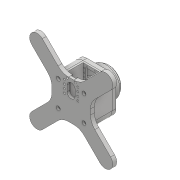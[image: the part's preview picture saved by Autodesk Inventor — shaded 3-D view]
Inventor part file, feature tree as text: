
AUTODESK INVENTOR PART (.ipt)
format: ipt  version: 2017 (Build 210142000, 142)  size: 484,864 bytes
history: native  units: mm
features: sketch x17, extrude x13, hole x4, fillet x2, projected_geometry x2, other x2, plane x1, split x1, chamfer x1, imported_body x1
ambient origin geometry x8: Origin, YZ Plane, XZ Plane, XY Plane, X Axis, Y Axis, Z Axis, Center Point
bodies: Solid1 (feature_tree)
feature tree (44):
  extrude  "Extrusion1"  Depth=24.5mm
  extrude  "Extrusion2"  Depth=33.0mm
  extrude  "Extrusion3"  Depth=16.0mm
  extrude  "Extrusion4"  Depth=70.0mm
  fillet  "Fillet1"  Radius=3.5mm
  extrude  "Extrusion5"  Depth=8.0mm TaperAngle=0.0deg
  extrude  "Extrusion6"  Depth=32.0mm
  fillet  "Fillet2"  Radius=12.0mm
  extrude  "Extrusion7"  Depth=19.25mm
  hole  "Hole1"  [1 undecoded]
  plane  "Work Plane1"
  split  "Split1"
  hole  "Hole2"  [1 undecoded]
  hole  "Hole3"  [1 undecoded]
  extrude  "Extrusion8"  Depth=33.0mm
  hole  "Hole4"  [1 undecoded]
  extrude  "Extrusion9"  Depth=16.0mm
  extrude  "Extrusion10"  Depth=27.0mm
  extrude  "Extrusion11"  Depth=36.0mm
  extrude  "Extrusion12"  Depth=8.0mm
  chamfer  "Chamfer1"  Distance=16.0mm
  extrude  "Extrusion13"  TaperAngle=0.0deg  [1 undecoded]
  sketch  "Sketch1"  dims[d0=21.0mm d1=24.5mm]
  sketch  "Sketch2"  dims[d2=6.0mm d3=33.0mm]
  sketch  "Sketch3"  dims[d4=6.0mm d5=16.0mm]
  sketch  "Sketch4"  dims[d6=6.0mm d7=70.0mm d8=3.5mm d9=0.0mm]
  sketch  "Sketch5"  dims[d10=42.0mm d11=8.0mm d12=0.0mm]
  projected_geometry  "Projected Loop2"
  sketch  "Sketch6"  dims[d13=8.0mm d14=0.0mm d15=32.0mm d16=12.0mm]
  imported_body  "base"
  sketch  "Sketch7"  dims[d17=32.0mm d18=0.0mm d19=19.25mm]
  sketch  "Sketch8"  dims[d20=0.0mm d21=0.0mm d22=45.0deg]
  projected_geometry  "Projected Loop3"
  sketch  "Sketch9"  dims[d23=30.0mm d24=45.0deg]
  sketch  "Sketch10"  dims[d25=30.0mm d26=8.0mm d27=0.0mm]
  sketch  "Sketch11"  dims[d28=30.0mm d29=33.0mm]
  sketch  "Sketch12"  dims[d30=6.0mm d31=20.0mm]
  sketch  "Sketch13"  dims[d32=3.0mm d33=0.0mm d34=16.0mm]
  sketch  "Sketch14"  dims[d35=9.0mm d36=27.0mm]
  sketch  "Sketch15"  dims[d37=36.0mm d38=6.75mm]
  sketch  "Sketch16"  dims[d39=8.0mm d40=8.0mm]
  sketch  "Sketch17"  dims[d41=8.0mm d42=16.0mm d43=2.0mm d44=6.0mm d45=4.0mm d46=6.0mm d47=90.0deg d48=8.0mm d49=20.594885mm d50=0.0mm d51=2.0mm d52=6.0mm d53=4.0mm d54=2.0mm d55=90.0deg d56=8.0mm d57=20.594885mm d58=52.0mm d59=52.0mm d60=12.0mm d61=6.0mm d62=4.0mm d63=2.0mm d64=90.0deg d65=8.0mm d66=20.594885mm d67=10.0mm d68=0.0mm d69=4.2mm d70=6.0mm d71=8.0mm d72=4.0mm d73=90.0deg d74=8.0mm d75=20.594885mm d76=7.1mm d77=7.1mm d78=5.0mm d79=0.0mm d80=59.0mm d81=17.5mm d82=0.0mm d83=52.0mm d84=7.0mm d85=0.0mm d86=47.0mm d87=23.0mm d88=0.0mm d89=1.5mm d90=2.0mm d91=45.0deg d92=16.0mm d93=12.0mm d94=12.0mm d95=10.0mm d96=0.0mm]
  other  "core"
  other  "top"
note: 5 required parameter values undecoded (feature->parameter linkage not recoverable at this tier; creation-order binding heuristic only, values carry confidence <= 0.55)
